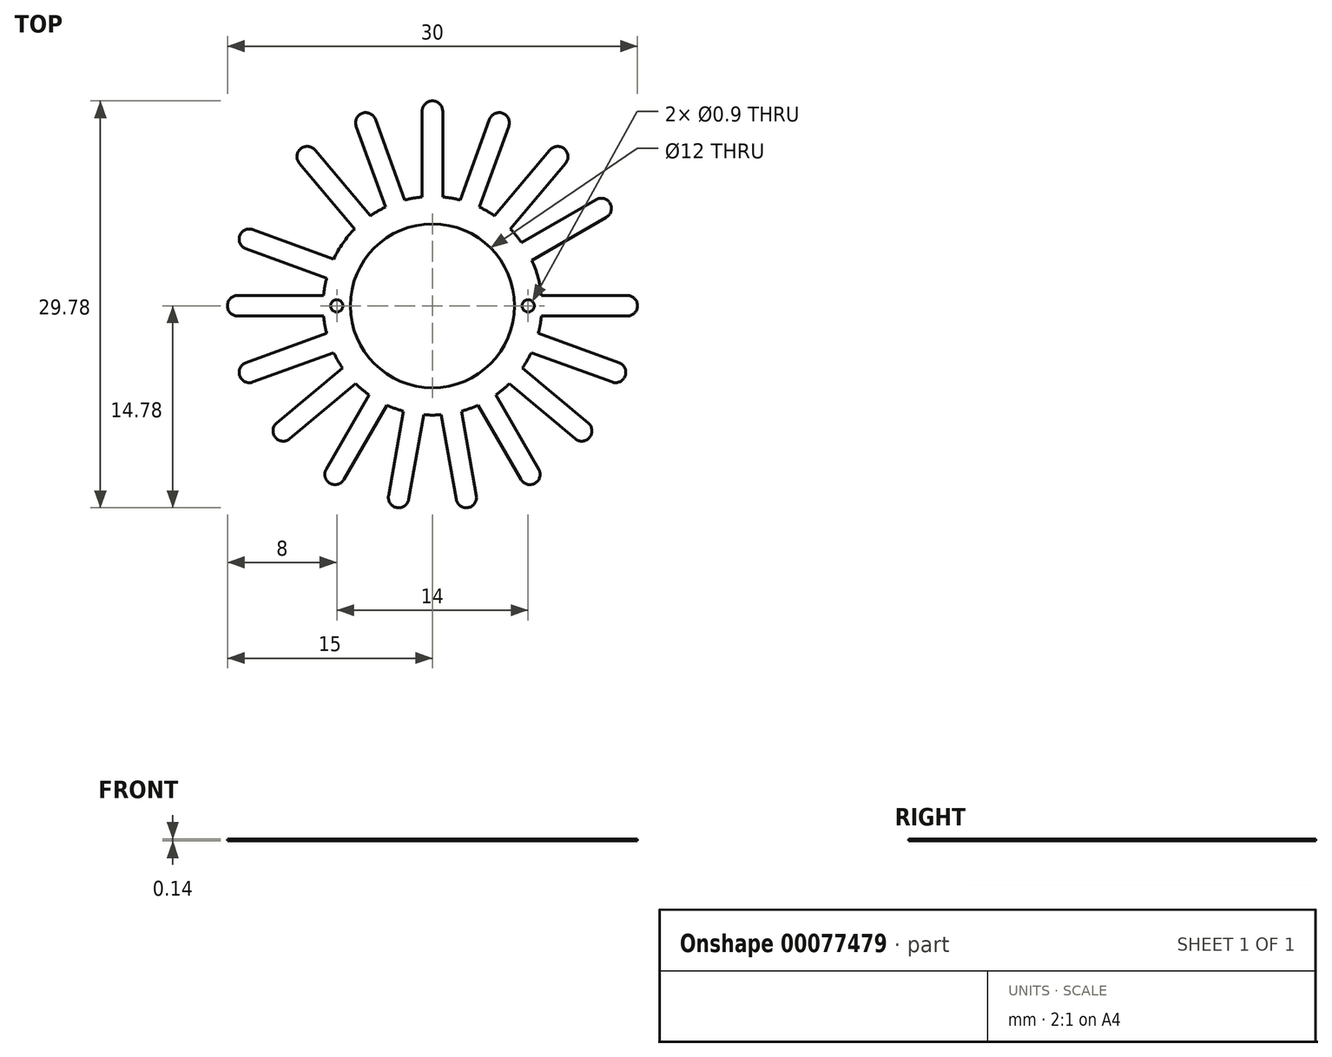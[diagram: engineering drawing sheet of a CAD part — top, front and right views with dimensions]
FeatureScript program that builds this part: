
annotation { "Feature Type Name" : "Feature", "Feature Type Description" : "" }
export const myFeature = defineFeature(function(context is Context, id is Id, definition is map)
    precondition{}
    {
        {
            var Q0;
            Q0=qCreatedBy(makeId("Top.planeOp"),FACE);
            var sketch = newSketch(context, id + "F0", { "sketchPlane" : qUnion([Q0])});
            skCircle(sketch, "E0", {"center": v(0, 0) * mm, "radius": 6 * mm});
            skCircle(sketch, "E1", {"center": v(0, 0) * mm, "radius": 8 * mm});
            skSolve(sketch);
        }
        {
            var Q0;
            Q0=makeQuery(id+"F0.imprint","IMPRINT",FACE,{"disambiguationData":[TD([[makeQuery(id+"F0.imprint","IMPRINT",EDGE,{"derivedFrom":sQuery(id+"F0.wireOp",EDGE,"E0")}),-1.0]])]});
            extrude(context, id + "F1", {"entities" : qUnion([Q0]), "depth" : 0.14 * mm});
        }
        {
            var Q0;
            Q0=qCreatedBy(makeId("Top.planeOp"),FACE);
            var sketch = newSketch(context, id + "F2", { "sketchPlane" : qUnion([Q0])});
            skCircle(sketch, "E2", {"center": v(0, 0) * mm, "radius": 8 * mm, "construction": true});
            skCircle(sketch, "E3", {"center": v(0, 0) * mm, "radius": 15 * mm, "construction": true});
            skArc(sketch, "E4", {"start": v(14.25, -0.75) * mm, "mid": v(15, 0) * mm, "end": v(14.25, 0.75) * mm});
            skLineSegment(sketch, "E5", {"start": v(14.25, -0.75) * mm, "end": v(7.96, -0.75) * mm});
            skLineSegment(sketch, "E6", {"start": v(14.25, 0.75) * mm, "end": v(7.96, 0.75) * mm});
            skLineSegment(sketch, "E7", {"start": v(7.96, 0.75) * mm, "end": v(7.96, -0.75) * mm});
            skSolve(sketch);
        }
        {
            var Q0;
            Q0=makeQuery(id+"F2.imprint","IMPRINT",FACE,{"disambiguationData":[TD([[makeQuery(id+"F2.imprint","IMPRINT",EDGE,{"derivedFrom":sQuery(id+"F2.wireOp",EDGE,"E4")}),1.0]])]});
            extrude(context, id + "F3", {"entities" : qUnion([Q0]), "depth" : 0.14 * mm});
        }
        {
            var Q0;
            Q0=qCreatedBy(makeId("Front.planeOp"),FACE);
            var sketch = newSketch(context, id + "F4", { "sketchPlane" : qUnion([Q0])});
            skLineSegment(sketch, "E8", {"start": v(0, 0) * mm, "end": v(0, 5.33) * mm, "construction": true});
            skSolve(sketch);
        }
        {
            var Q0;
            Q0=makeQuery(id+"F3.opExtrude","SWEPT_BODY",BODY,{"disambiguationData":[OSD([sQuery(id+"F2.wireOp",EDGE,"E4"),sQuery(id+"F2.wireOp",EDGE,"E5"),sQuery(id+"F2.wireOp",EDGE,"E6"),sQuery(id+"F2.wireOp",EDGE,"E7")])]});
            var Q1;
            Q1=sQuery(id+"F4.wireOp",EDGE,"E8");
            circularPattern(context, id + "F5", {"entities" : qUnion([Q0]), "axis" : qUnion([Q1]), "angle" : 20 * degree, "instanceCount" : 11, "oppositeDirection" : true});
        }
        {
            var Q0;
            Q0=qCreatedBy(makeId("Top.planeOp"),FACE);
            var sketch = newSketch(context, id + "F6", { "sketchPlane" : qUnion([Q0])});
            skCircle(sketch, "E9", {"center": v(0, 0) * mm, "radius": 15 * mm, "construction": true});
            skLineSegment(sketch, "E10", {"start": v(0, 0) * mm, "end": v(13, 7.5) * mm, "construction": true});
            skLineSegment(sketch, "E11", {"start": v(0, 0) * mm, "end": v(13.86, 0) * mm, "construction": true});
            skArc(sketch, "E12", {"start": v(12.72, 6.48) * mm, "mid": v(13, 7.5) * mm, "end": v(11.97, 7.77) * mm});
            skLineSegment(sketch, "E13", {"start": v(12.34, 7.13) * mm, "end": v(12.72, 6.48) * mm});
            skLineSegment(sketch, "E14", {"start": v(12.72, 6.48) * mm, "end": v(6.65, 2.98) * mm});
            skLineSegment(sketch, "E15", {"start": v(6.65, 2.98) * mm, "end": v(5.9, 4.27) * mm});
            skLineSegment(sketch, "E16", {"start": v(5.9, 4.27) * mm, "end": v(11.97, 7.77) * mm});
            skSolve(sketch);
        }
        {
            var Q0;
            Q0=makeQuery(id+"F6.imprint","IMPRINT",FACE,{"disambiguationData":[TD([[makeQuery(id+"F6.imprint","IMPRINT",EDGE,{"derivedFrom":sQuery(id+"F6.wireOp",EDGE,"E12")}),1.0]])]});
            extrude(context, id + "F7", {"entities" : qUnion([Q0]), "depth" : 0.14 * mm});
        }
        {
            var Q0;
            Q0=makeQuery(id+"F7.opExtrude","SWEPT_BODY",BODY,{"disambiguationData":[OSD([sQuery(id+"F6.wireOp",EDGE,"E12"),sQuery(id+"F6.wireOp",EDGE,"E14"),sQuery(id+"F6.wireOp",EDGE,"E15"),sQuery(id+"F6.wireOp",EDGE,"E16")])]});
            var Q1;
            Q1=sQuery(id+"F4.wireOp",EDGE,"E8");
            circularPattern(context, id + "F8", {"entities" : qUnion([Q0]), "axis" : qUnion([Q1]), "angle" : 20 * degree, "instanceCount" : 6});
        }
        {
            var Q0;
            Q0=makeQuery(id+"F1.opExtrude","SWEPT_BODY",BODY,{"disambiguationData":[OSD([sQuery(id+"F0.wireOp",EDGE,"E0"),sQuery(id+"F0.wireOp",EDGE,"E1")])]});
            var Q1;
            Q1=makeQuery(id+"F7.opExtrude","SWEPT_BODY",BODY,{"disambiguationData":[OSD([sQuery(id+"F6.wireOp",EDGE,"E12"),sQuery(id+"F6.wireOp",EDGE,"E14"),sQuery(id+"F6.wireOp",EDGE,"E15"),sQuery(id+"F6.wireOp",EDGE,"E16")])]});
            var Q2;
            Q2=makeQuery(id+"F8.opPattern","COPY",BODY,{"derivedFrom":makeQuery(id+"F7.opExtrude","SWEPT_BODY",BODY,{"disambiguationData":[OSD([sQuery(id+"F6.wireOp",EDGE,"E12"),sQuery(id+"F6.wireOp",EDGE,"E14"),sQuery(id+"F6.wireOp",EDGE,"E15"),sQuery(id+"F6.wireOp",EDGE,"E16")])]}),"instanceName":"1"});
            var Q3;
            Q3=makeQuery(id+"F8.opPattern","COPY",BODY,{"derivedFrom":makeQuery(id+"F7.opExtrude","SWEPT_BODY",BODY,{"disambiguationData":[OSD([sQuery(id+"F6.wireOp",EDGE,"E12"),sQuery(id+"F6.wireOp",EDGE,"E14"),sQuery(id+"F6.wireOp",EDGE,"E15"),sQuery(id+"F6.wireOp",EDGE,"E16")])]}),"instanceName":"2"});
            var Q4;
            Q4=makeQuery(id+"F8.opPattern","COPY",BODY,{"derivedFrom":makeQuery(id+"F7.opExtrude","SWEPT_BODY",BODY,{"disambiguationData":[OSD([sQuery(id+"F6.wireOp",EDGE,"E12"),sQuery(id+"F6.wireOp",EDGE,"E14"),sQuery(id+"F6.wireOp",EDGE,"E15"),sQuery(id+"F6.wireOp",EDGE,"E16")])]}),"instanceName":"3"});
            var Q5;
            Q5=makeQuery(id+"F8.opPattern","COPY",BODY,{"derivedFrom":makeQuery(id+"F7.opExtrude","SWEPT_BODY",BODY,{"disambiguationData":[OSD([sQuery(id+"F6.wireOp",EDGE,"E12"),sQuery(id+"F6.wireOp",EDGE,"E14"),sQuery(id+"F6.wireOp",EDGE,"E15"),sQuery(id+"F6.wireOp",EDGE,"E16")])]}),"instanceName":"4"});
            var Q6;
            Q6=makeQuery(id+"F8.opPattern","COPY",BODY,{"derivedFrom":makeQuery(id+"F7.opExtrude","SWEPT_BODY",BODY,{"disambiguationData":[OSD([sQuery(id+"F6.wireOp",EDGE,"E12"),sQuery(id+"F6.wireOp",EDGE,"E14"),sQuery(id+"F6.wireOp",EDGE,"E15"),sQuery(id+"F6.wireOp",EDGE,"E16")])]}),"instanceName":"5"});
            var Q7;
            Q7=makeQuery(id+"F5.opPattern","COPY",BODY,{"derivedFrom":makeQuery(id+"F3.opExtrude","SWEPT_BODY",BODY,{"disambiguationData":[OSD([sQuery(id+"F2.wireOp",EDGE,"E4"),sQuery(id+"F2.wireOp",EDGE,"E5"),sQuery(id+"F2.wireOp",EDGE,"E6"),sQuery(id+"F2.wireOp",EDGE,"E7")])]}),"instanceName":"10"});
            var Q8;
            Q8=makeQuery(id+"F5.opPattern","COPY",BODY,{"derivedFrom":makeQuery(id+"F3.opExtrude","SWEPT_BODY",BODY,{"disambiguationData":[OSD([sQuery(id+"F2.wireOp",EDGE,"E4"),sQuery(id+"F2.wireOp",EDGE,"E5"),sQuery(id+"F2.wireOp",EDGE,"E6"),sQuery(id+"F2.wireOp",EDGE,"E7")])]}),"instanceName":"9"});
            var Q9;
            Q9=makeQuery(id+"F5.opPattern","COPY",BODY,{"derivedFrom":makeQuery(id+"F3.opExtrude","SWEPT_BODY",BODY,{"disambiguationData":[OSD([sQuery(id+"F2.wireOp",EDGE,"E4"),sQuery(id+"F2.wireOp",EDGE,"E5"),sQuery(id+"F2.wireOp",EDGE,"E6"),sQuery(id+"F2.wireOp",EDGE,"E7")])]}),"instanceName":"8"});
            var Q10;
            Q10=makeQuery(id+"F5.opPattern","COPY",BODY,{"derivedFrom":makeQuery(id+"F3.opExtrude","SWEPT_BODY",BODY,{"disambiguationData":[OSD([sQuery(id+"F2.wireOp",EDGE,"E4"),sQuery(id+"F2.wireOp",EDGE,"E5"),sQuery(id+"F2.wireOp",EDGE,"E6"),sQuery(id+"F2.wireOp",EDGE,"E7")])]}),"instanceName":"7"});
            var Q11;
            Q11=makeQuery(id+"F5.opPattern","COPY",BODY,{"derivedFrom":makeQuery(id+"F3.opExtrude","SWEPT_BODY",BODY,{"disambiguationData":[OSD([sQuery(id+"F2.wireOp",EDGE,"E4"),sQuery(id+"F2.wireOp",EDGE,"E5"),sQuery(id+"F2.wireOp",EDGE,"E6"),sQuery(id+"F2.wireOp",EDGE,"E7")])]}),"instanceName":"6"});
            var Q12;
            Q12=makeQuery(id+"F5.opPattern","COPY",BODY,{"derivedFrom":makeQuery(id+"F3.opExtrude","SWEPT_BODY",BODY,{"disambiguationData":[OSD([sQuery(id+"F2.wireOp",EDGE,"E4"),sQuery(id+"F2.wireOp",EDGE,"E5"),sQuery(id+"F2.wireOp",EDGE,"E6"),sQuery(id+"F2.wireOp",EDGE,"E7")])]}),"instanceName":"4"});
            var Q13;
            Q13=makeQuery(id+"F5.opPattern","COPY",BODY,{"derivedFrom":makeQuery(id+"F3.opExtrude","SWEPT_BODY",BODY,{"disambiguationData":[OSD([sQuery(id+"F2.wireOp",EDGE,"E4"),sQuery(id+"F2.wireOp",EDGE,"E5"),sQuery(id+"F2.wireOp",EDGE,"E6"),sQuery(id+"F2.wireOp",EDGE,"E7")])]}),"instanceName":"5"});
            var Q14;
            Q14=makeQuery(id+"F5.opPattern","COPY",BODY,{"derivedFrom":makeQuery(id+"F3.opExtrude","SWEPT_BODY",BODY,{"disambiguationData":[OSD([sQuery(id+"F2.wireOp",EDGE,"E4"),sQuery(id+"F2.wireOp",EDGE,"E5"),sQuery(id+"F2.wireOp",EDGE,"E6"),sQuery(id+"F2.wireOp",EDGE,"E7")])]}),"instanceName":"3"});
            var Q15;
            Q15=makeQuery(id+"F5.opPattern","COPY",BODY,{"derivedFrom":makeQuery(id+"F3.opExtrude","SWEPT_BODY",BODY,{"disambiguationData":[OSD([sQuery(id+"F2.wireOp",EDGE,"E4"),sQuery(id+"F2.wireOp",EDGE,"E5"),sQuery(id+"F2.wireOp",EDGE,"E6"),sQuery(id+"F2.wireOp",EDGE,"E7")])]}),"instanceName":"2"});
            var Q16;
            Q16=makeQuery(id+"F5.opPattern","COPY",BODY,{"derivedFrom":makeQuery(id+"F3.opExtrude","SWEPT_BODY",BODY,{"disambiguationData":[OSD([sQuery(id+"F2.wireOp",EDGE,"E4"),sQuery(id+"F2.wireOp",EDGE,"E5"),sQuery(id+"F2.wireOp",EDGE,"E6"),sQuery(id+"F2.wireOp",EDGE,"E7")])]}),"instanceName":"1"});
            var Q17;
            Q17=makeQuery(id+"F3.opExtrude","SWEPT_BODY",BODY,{"disambiguationData":[OSD([sQuery(id+"F2.wireOp",EDGE,"E4"),sQuery(id+"F2.wireOp",EDGE,"E5"),sQuery(id+"F2.wireOp",EDGE,"E6"),sQuery(id+"F2.wireOp",EDGE,"E7")])]});
            booleanBodies(context, id + "F9", {"operationType" : BooleanOperationType.UNION, "tools" : qUnion([Q0, Q1, Q2, Q3, Q4, Q5, Q6, Q7, Q8, Q9, Q10, Q11, Q12, Q13, Q14, Q15, Q16, Q17])});
        }
        {
            var Q0;
            {var subQ0=makeQuery(id+"F3.opExtrude","CAP_FACE",FACE,{"disambiguationData":[OSD([sQuery(id+"F2.wireOp",EDGE,"E4"),sQuery(id+"F2.wireOp",EDGE,"E5"),sQuery(id+"F2.wireOp",EDGE,"E6"),sQuery(id+"F2.wireOp",EDGE,"E7")])],"isStart":false});var subQ1=makeQuery(id+"F7.opExtrude","CAP_FACE",FACE,{"disambiguationData":[OSD([sQuery(id+"F6.wireOp",EDGE,"E12"),sQuery(id+"F6.wireOp",EDGE,"E14"),sQuery(id+"F6.wireOp",EDGE,"E15"),sQuery(id+"F6.wireOp",EDGE,"E16")])],"isStart":false});Q0=makeQuery(id+"F9.opBoolean","MERGE",FACE,{"derivedFrom":[makeQuery(id+"F1.opExtrude","CAP_FACE",FACE,{"disambiguationData":[OSD([sQuery(id+"F0.wireOp",EDGE,"E0"),sQuery(id+"F0.wireOp",EDGE,"E1")])],"isStart":false}),subQ0,makeQuery(id+"F5.opPattern","COPY",FACE,{"derivedFrom":subQ0,"instanceName":"1"}),makeQuery(id+"F5.opPattern","COPY",FACE,{"derivedFrom":subQ0,"instanceName":"2"}),makeQuery(id+"F5.opPattern","COPY",FACE,{"derivedFrom":subQ0,"instanceName":"3"}),makeQuery(id+"F5.opPattern","COPY",FACE,{"derivedFrom":subQ0,"instanceName":"4"}),makeQuery(id+"F5.opPattern","COPY",FACE,{"derivedFrom":subQ0,"instanceName":"5"}),makeQuery(id+"F5.opPattern","COPY",FACE,{"derivedFrom":subQ0,"instanceName":"6"}),makeQuery(id+"F5.opPattern","COPY",FACE,{"derivedFrom":subQ0,"instanceName":"7"}),makeQuery(id+"F5.opPattern","COPY",FACE,{"derivedFrom":subQ0,"instanceName":"8"}),makeQuery(id+"F5.opPattern","COPY",FACE,{"derivedFrom":subQ0,"instanceName":"9"}),makeQuery(id+"F5.opPattern","COPY",FACE,{"derivedFrom":subQ0,"instanceName":"10"}),subQ1,makeQuery(id+"F8.opPattern","COPY",FACE,{"derivedFrom":subQ1,"instanceName":"1"}),makeQuery(id+"F8.opPattern","COPY",FACE,{"derivedFrom":subQ1,"instanceName":"2"}),makeQuery(id+"F8.opPattern","COPY",FACE,{"derivedFrom":subQ1,"instanceName":"3"}),makeQuery(id+"F8.opPattern","COPY",FACE,{"derivedFrom":subQ1,"instanceName":"4"}),makeQuery(id+"F8.opPattern","COPY",FACE,{"derivedFrom":subQ1,"instanceName":"5"})]});}
            var sketch = newSketch(context, id + "F10", { "sketchPlane" : qUnion([Q0])});
            skCircle(sketch, "E17", {"center": v(0, 0) * mm, "radius": 7 * mm, "construction": true});
            skCircle(sketch, "E18", {"center": v(7, 0) * mm, "radius": 0.45 * mm});
            skCircle(sketch, "E19", {"center": v(-7, 0) * mm, "radius": 0.45 * mm});
            skSolve(sketch);
        }
        {
            var Q0;
            {Q0=qUnion([makeQuery(id+"F10.imprint","IMPRINT",FACE,{"disambiguationData":[TD([[makeQuery(id+"F10.imprint","IMPRINT",EDGE,{"derivedFrom":sQuery(id+"F10.wireOp",EDGE,"E18")}),1.0]])]}),makeQuery(id+"F10.imprint","IMPRINT",FACE,{"disambiguationData":[TD([[makeQuery(id+"F10.imprint","IMPRINT",EDGE,{"derivedFrom":sQuery(id+"F10.wireOp",EDGE,"E19")}),1.0]])]})]);}
            extrude(context, id + "F11", {"entities" : qUnion([Q0]), "operationType" : NewBodyOperationType.REMOVE, "oppositeDirection" : true, "depth" : 0.14 * mm});
        }
    });
